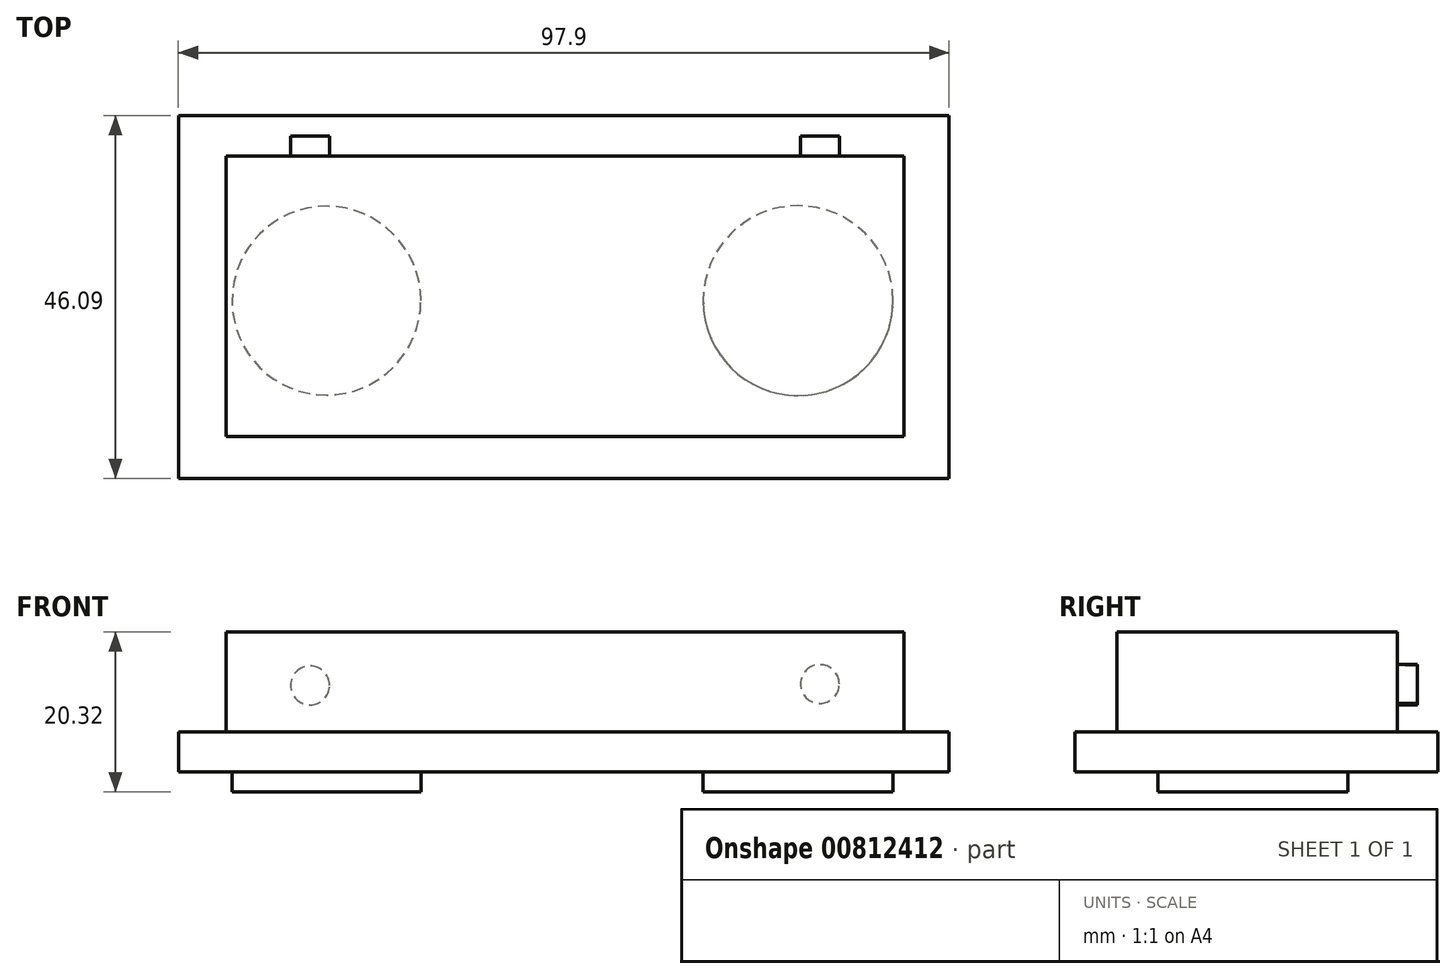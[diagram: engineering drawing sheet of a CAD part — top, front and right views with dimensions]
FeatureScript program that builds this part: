
annotation { "Feature Type Name" : "Feature", "Feature Type Description" : "" }
export const myFeature = defineFeature(function(context is Context, id is Id, definition is map)
    precondition{}
    {
        {
            var Q0;
            Q0=qCreatedBy(makeId("Top.planeOp"),FACE);
            var sketch = newSketch(context, id + "F0", { "sketchPlane" : qUnion([Q0])});
            skLineSegment(sketch, "E0.bottom", {"start": v(-47.66, 23.5) * mm, "end": v(50.24, 23.5) * mm});
            skLineSegment(sketch, "E0.top", {"start": v(-47.66, -22.58) * mm, "end": v(50.24, -22.58) * mm});
            skLineSegment(sketch, "E0.left", {"start": v(-47.66, 23.5) * mm, "end": v(-47.66, -22.58) * mm});
            skLineSegment(sketch, "E0.right", {"start": v(50.24, 23.5) * mm, "end": v(50.24, -22.58) * mm});
            skSolve(sketch);
        }
        {
            var Q0;
            Q0 = qSketchRegion(id + "F0", true);
            extrude(context, id + "F1", {"entities" : qUnion([Q0]), "depth" : 5.08 * mm, "offsetDistance" : 25.4 * mm});
        }
        {
            var Q0;
            Q0=makeQuery(id+"F1.opExtrude","CAP_FACE",FACE,{"disambiguationData":[OSD([sQuery(id+"F0.wireOp",EDGE,"E0.bottom"),sQuery(id+"F0.wireOp",EDGE,"E0.top"),sQuery(id+"F0.wireOp",EDGE,"E0.left"),sQuery(id+"F0.wireOp",EDGE,"E0.right")])],"isStart":false});
            var sketch = newSketch(context, id + "F2", { "sketchPlane" : qUnion([Q0])});
            skLineSegment(sketch, "E1.bottom", {"start": v(-41.57, 18.34) * mm, "end": v(44.52, 18.34) * mm});
            skLineSegment(sketch, "E1.top", {"start": v(-41.57, -17.24) * mm, "end": v(44.52, -17.24) * mm});
            skLineSegment(sketch, "E1.left", {"start": v(-41.57, 18.34) * mm, "end": v(-41.57, -17.24) * mm});
            skLineSegment(sketch, "E1.right", {"start": v(44.52, 18.34) * mm, "end": v(44.52, -17.24) * mm});
            skSolve(sketch);
        }
        {
            var Q0;
            Q0=makeQuery(id+"F2.imprint","IMPRINT",FACE,{"disambiguationData":[TD([[makeQuery(id+"F2.imprint","IMPRINT",EDGE,{"derivedFrom":sQuery(id+"F2.wireOp",EDGE,"E1.bottom")}),-1.0]])]});
            extrude(context, id + "F3", {"entities" : qUnion([Q0]), "operationType" : NewBodyOperationType.ADD, "depth" : 12.7 * mm, "offsetDistance" : 25.4 * mm});
        }
        {
            var Q0;
            Q0=makeQuery(id+"F1.opExtrude","CAP_FACE",FACE,{"disambiguationData":[OSD([sQuery(id+"F0.wireOp",EDGE,"E0.bottom"),sQuery(id+"F0.wireOp",EDGE,"E0.top"),sQuery(id+"F0.wireOp",EDGE,"E0.left"),sQuery(id+"F0.wireOp",EDGE,"E0.right")])],"isStart":true});
            var sketch = newSketch(context, id + "F4", { "sketchPlane" : qUnion([Q0])});
            skCircle(sketch, "E2", {"center": v(-28.85, 0) * mm, "radius": 12 * mm});
            skCircle(sketch, "E3", {"center": v(31.06, 0) * mm, "radius": 12.06 * mm});
            skSolve(sketch);
        }
        {
            var Q0;
            Q0=makeQuery(id+"F4.imprint","IMPRINT",FACE,{"disambiguationData":[TD([[makeQuery(id+"F4.imprint","IMPRINT",EDGE,{"derivedFrom":sQuery(id+"F4.wireOp",EDGE,"E2")}),1.0]])]});
            var Q1;
            Q1=makeQuery(id+"F4.imprint","IMPRINT",FACE,{"disambiguationData":[TD([[makeQuery(id+"F4.imprint","IMPRINT",EDGE,{"derivedFrom":sQuery(id+"F4.wireOp",EDGE,"E3")}),1.0]])]});
            extrude(context, id + "F5", {"entities" : qUnion([Q0, Q1]), "operationType" : NewBodyOperationType.ADD, "depth" : 2.54 * mm, "offsetDistance" : 25.4 * mm});
        }
        {
            var Q0;
            Q0=makeQuery(id+"F3.opExtrude","SWEPT_FACE",FACE,{"disambiguationData":[OSD([sQuery(id+"F2.wireOp",EDGE,"E1.bottom")])]});
            var sketch = newSketch(context, id + "F6", { "sketchPlane" : qUnion([Q0])});
            skCircle(sketch, "E4", {"center": v(30.93, 10.98) * mm, "radius": 2.47 * mm});
            skCircle(sketch, "E5", {"center": v(-33.83, 11.15) * mm, "radius": 2.47 * mm});
            skSolve(sketch);
        }
        {
            var Q0;
            Q0=makeQuery(id+"F6.imprint","IMPRINT",FACE,{"disambiguationData":[TD([[makeQuery(id+"F6.imprint","IMPRINT",EDGE,{"derivedFrom":sQuery(id+"F6.wireOp",EDGE,"E4")}),1.0]])]});
            var Q1;
            Q1=makeQuery(id+"F6.imprint","IMPRINT",FACE,{"disambiguationData":[TD([[makeQuery(id+"F6.imprint","IMPRINT",EDGE,{"derivedFrom":sQuery(id+"F6.wireOp",EDGE,"E5")}),1.0]])]});
            var Q2;
            Q2=sQuery(id+"F6.wireOp",EDGE,"E4");
            var Q3;
            Q3=sQuery(id+"F6.wireOp",EDGE,"E5");
            extrude(context, id + "F7", {"entities" : qUnion([Q0, Q1]), "surfaceEntities" : qUnion([Q2, Q3]), "depth" : 2.54 * mm, "offsetDistance" : 25.4 * mm});
        }
    });
